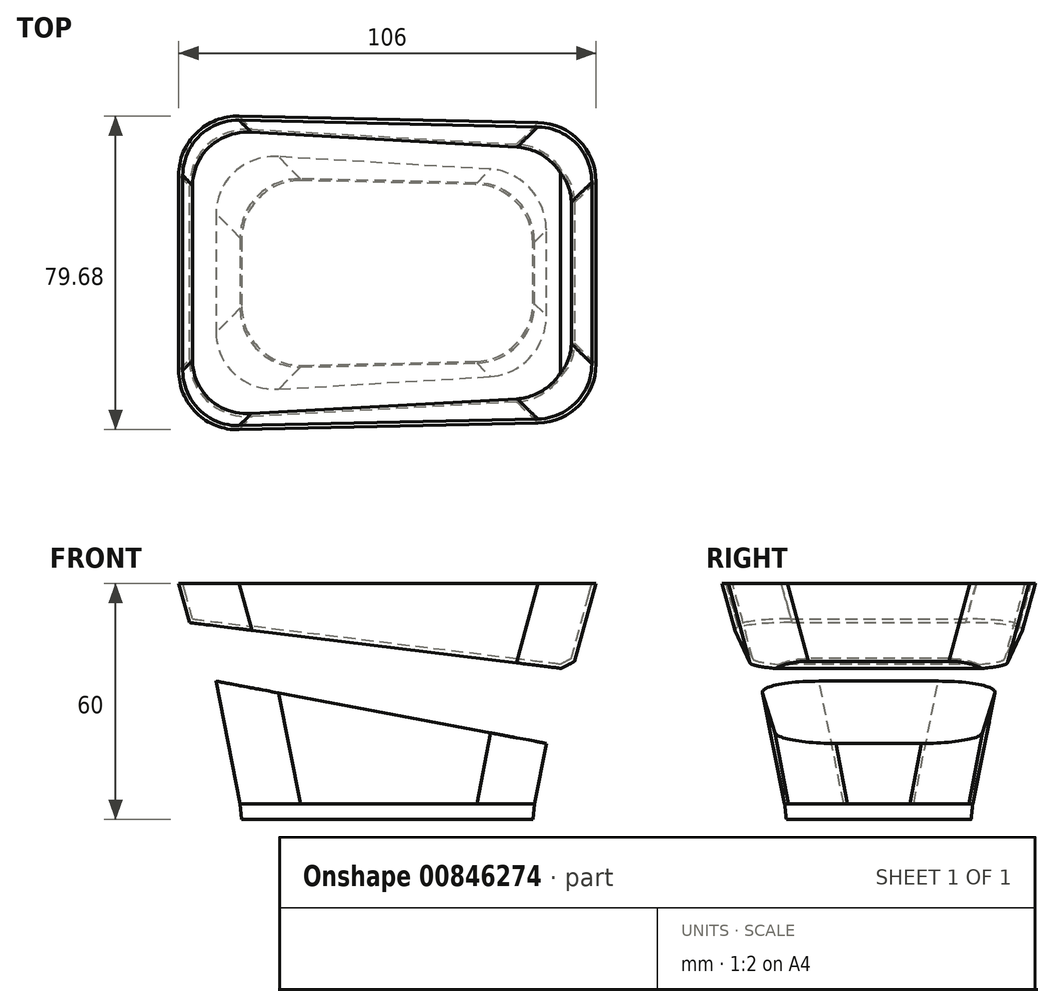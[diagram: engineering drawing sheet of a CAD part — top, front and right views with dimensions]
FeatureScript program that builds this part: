
annotation { "Feature Type Name" : "Feature", "Feature Type Description" : "" }
export const myFeature = defineFeature(function(context is Context, id is Id, definition is map)
    precondition{}
    {
        {
            var Q0;
            Q0=qCreatedBy(makeId("Top.planeOp"),FACE);
            var sketch = newSketch(context, id + "F0", { "sketchPlane" : qUnion([Q0])});
            skLineSegment(sketch, "E0", {"start": v(-45, 32) * mm, "end": v(-45, -32) * mm});
            skLineSegment(sketch, "E1", {"start": v(-45, -32) * mm, "end": v(45, -30) * mm});
            skLineSegment(sketch, "E2", {"start": v(45, -30) * mm, "end": v(45, 30) * mm});
            skLineSegment(sketch, "E3", {"start": v(45, 30) * mm, "end": v(-45, 32) * mm});
            skLineSegment(sketch, "E4.0", {"start": v(22.33, 22.5) * mm, "end": v(-21.67, 23.48) * mm});
            skLineSegment(sketch, "E4.1", {"start": v(37, -7.5) * mm, "end": v(37, 7.5) * mm});
            skLineSegment(sketch, "E4.2", {"start": v(-21.67, -23.48) * mm, "end": v(22.33, -22.5) * mm});
            skLineSegment(sketch, "E4.3", {"start": v(-37, 8.48) * mm, "end": v(-37, -8.48) * mm});
            skPoint(sketch, "E5.visualSharp", {"position": v(-37, 23.82) * mm});
            skArc(sketch, "E5.filletArc", {"start": v(-21.67, 23.48) * mm, "mid": v(-32.49, 19.2) * mm, "end": v(-37, 8.48) * mm});
            skPoint(sketch, "E6.visualSharp", {"position": v(-37, -23.82) * mm});
            skArc(sketch, "E6.filletArc", {"start": v(-37, -8.48) * mm, "mid": v(-32.49, -19.2) * mm, "end": v(-21.67, -23.48) * mm});
            skPoint(sketch, "E7.visualSharp", {"position": v(37, 22.18) * mm});
            skArc(sketch, "E7.filletArc", {"start": v(37, 7.5) * mm, "mid": v(32.72, 18) * mm, "end": v(22.33, 22.5) * mm});
            skPoint(sketch, "E8.visualSharp", {"position": v(37, -22.18) * mm});
            skArc(sketch, "E8.filletArc", {"start": v(22.33, -22.5) * mm, "mid": v(32.72, -18) * mm, "end": v(37, -7.5) * mm});
            skSolve(sketch);
        }
        {
            var Q0;
            Q0=qCreatedBy(makeId("Top.planeOp"),FACE);
            cPlane(context, id + "F1", {"entities" : qUnion([Q0]), "cplaneType" : CPlaneType.OFFSET, "offset" : 60 * mm, "width" : 150 * mm, "height" : 150 * mm});
        }
        {
            var Q0;
            Q0=qCreatedBy(id+"F1.planeOp",FACE);
            var sketch = newSketch(context, id + "F2", { "sketchPlane" : qUnion([Q0])});
            skLineSegment(sketch, "E9.1", {"start": v(38.33, 38.15) * mm, "end": v(-37.67, 39.84) * mm});
            skLineSegment(sketch, "E9.2", {"start": v(-53, 24.84) * mm, "end": v(-53, -24.84) * mm});
            skLineSegment(sketch, "E9.5", {"start": v(-37.67, -39.84) * mm, "end": v(38.33, -38.15) * mm});
            skLineSegment(sketch, "E9.7", {"start": v(53, -23.15) * mm, "end": v(53, 23.15) * mm});
            skPoint(sketch, "E10.visualSharp", {"position": v(-53, 40.18) * mm});
            skArc(sketch, "E10.filletArc", {"start": v(-37.67, 39.84) * mm, "mid": v(-48.49, 35.57) * mm, "end": v(-53, 24.84) * mm});
            skPoint(sketch, "E11.visualSharp", {"position": v(53, 37.82) * mm});
            skArc(sketch, "E11.filletArc", {"start": v(53, 23.15) * mm, "mid": v(48.72, 33.64) * mm, "end": v(38.33, 38.15) * mm});
            skPoint(sketch, "E12.visualSharp", {"position": v(53, -37.82) * mm});
            skArc(sketch, "E12.filletArc", {"start": v(38.33, -38.15) * mm, "mid": v(48.72, -33.64) * mm, "end": v(53, -23.15) * mm});
            skPoint(sketch, "E13.visualSharp", {"position": v(-53, -40.18) * mm});
            skArc(sketch, "E13.filletArc", {"start": v(-53, -24.84) * mm, "mid": v(-48.49, -35.57) * mm, "end": v(-37.67, -39.84) * mm});
            skSolve(sketch);
        }
        {
            var Q0;
            Q0=qCreatedBy(makeId("Front.planeOp"),FACE);
            var sketch = newSketch(context, id + "F3", { "sketchPlane" : qUnion([Q0])});
            skLineSegment(sketch, "E14", {"start": v(-37, 0) * mm, "end": v(-37.4, 4) * mm});
            skLineSegment(sketch, "E15", {"start": v(-37.4, 4) * mm, "end": v(-46.35, 49.51) * mm});
            skLineSegment(sketch, "E16", {"start": v(37, 0) * mm, "end": v(-37, 0) * mm});
            skLineSegment(sketch, "E17", {"start": v(-50.32, 50) * mm, "end": v(-53, 60) * mm});
            skLineSegment(sketch, "E18", {"start": v(-53, 60) * mm, "end": v(53, 60) * mm});
            skLineSegment(sketch, "E19", {"start": v(53, 60) * mm, "end": v(47.1, 38) * mm});
            skLineSegment(sketch, "E20", {"start": v(-50.32, 50) * mm, "end": v(47.1, 38) * mm});
            skLineSegment(sketch, "E21", {"start": v(37.4, 4) * mm, "end": v(37, 0) * mm});
            skLineSegment(sketch, "E22", {"start": v(44.16, 38.36) * mm, "end": v(37.4, 4) * mm});
            skLineSegment(sketch, "E23", {"start": v(-37.4, 4) * mm, "end": v(37.4, 4) * mm});
            skLineSegment(sketch, "E24", {"start": v(-50.32, 50) * mm, "end": v(-64.72, 39.12) * mm});
            skLineSegment(sketch, "E25", {"start": v(-64.72, 39.12) * mm, "end": v(67.69, 14.16) * mm});
            skLineSegment(sketch, "E26", {"start": v(67.69, 14.16) * mm, "end": v(47.1, 38) * mm});
            skLineSegment(sketch, "E27", {"start": v(44.16, 38.36) * mm, "end": v(47.7, 40.22) * mm});
            skSolve(sketch);
        }
        {
            var Q0;
            Q0=sQuery(id+"F3.wireOp",EDGE,"E23");
            var Q1;
            Q1=qCreatedBy(makeId("Top.planeOp"),FACE);
            cPlane(context, id + "F4", {"entities" : qUnion([Q0, Q1]), "cplaneType" : CPlaneType.LINE_ANGLE, "offset" : 25 * mm, "angle" : 0 * degree, "width" : 150 * mm, "height" : 150 * mm});
        }
        {
            var Q0;
            Q0=qCreatedBy(id+"F4.planeOp",FACE);
            var sketch = newSketch(context, id + "F5", { "sketchPlane" : qUnion([Q0])});
            skLineSegment(sketch, "E28.0", {"start": v(-37.4, -8.9) * mm, "end": v(-37.4, 8.9) * mm});
            skLineSegment(sketch, "E29.0", {"start": v(22.73, -22.9) * mm, "end": v(-22.07, -23.89) * mm});
            skLineSegment(sketch, "E30.0", {"start": v(37.4, 7.9) * mm, "end": v(37.4, -7.9) * mm});
            skLineSegment(sketch, "E31.0", {"start": v(-22.07, 23.89) * mm, "end": v(22.73, 22.9) * mm});
            skPoint(sketch, "E32.visualSharp", {"position": v(-37.4, -24.23) * mm});
            skArc(sketch, "E32.filletArc", {"start": v(-37.4, -8.9) * mm, "mid": v(-32.89, -19.62) * mm, "end": v(-22.07, -23.89) * mm});
            skPoint(sketch, "E33.visualSharp", {"position": v(37.4, -22.57) * mm});
            skArc(sketch, "E33.filletArc", {"start": v(22.73, -22.9) * mm, "mid": v(33.12, -18.38) * mm, "end": v(37.4, -7.9) * mm});
            skPoint(sketch, "E34.visualSharp", {"position": v(37.4, 22.57) * mm});
            skArc(sketch, "E34.filletArc", {"start": v(37.4, 7.9) * mm, "mid": v(33.12, 18.38) * mm, "end": v(22.73, 22.9) * mm});
            skPoint(sketch, "E35.visualSharp", {"position": v(-37.4, 24.23) * mm});
            skArc(sketch, "E35.filletArc", {"start": v(-22.07, 23.89) * mm, "mid": v(-32.89, 19.62) * mm, "end": v(-37.4, 8.9) * mm});
            skSolve(sketch);
        }
        {
            var Q0;
            Q0=makeQuery(id+"F0.imprint","IMPRINT",FACE,{"disambiguationData":[TD([[makeQuery(id+"F0.imprint","IMPRINT",EDGE,{"derivedFrom":sQuery(id+"F0.wireOp",EDGE,"E4.0")}),1.0]])]});
            var Q1;
            Q1=makeQuery(id+"F5.imprint","IMPRINT",FACE,{"disambiguationData":[TD([[makeQuery(id+"F5.imprint","IMPRINT",EDGE,{"derivedFrom":sQuery(id+"F5.wireOp",EDGE,"E28.0")}),-1.0]])]});
            loft(context, id + "F6", {"sheetProfilesArray" : [{ "sheetProfileEntities" : qUnion([Q0]) }, { "sheetProfileEntities" : qUnion([Q1]) }]});
        }
        {
            var Q0;
            Q0=sQuery(id+"F3.wireOp",VERTEX,"E15.end");
            var Q1;
            Q1=qCreatedBy(makeId("Top.planeOp"),FACE);
            cPlane(context, id + "F7", {"entities" : qUnion([Q0, Q1]), "cplaneType" : CPlaneType.PLANE_POINT, "offset" : 25 * mm, "width" : 150 * mm, "height" : 150 * mm});
        }
        {
            var Q0;
            Q0=qCreatedBy(id+"F7.planeOp",FACE);
            var sketch = newSketch(context, id + "F8", { "sketchPlane" : qUnion([Q0])});
            skLineSegment(sketch, "E36.0", {"start": v(-46.32, 18.01) * mm, "end": v(-46.32, -18.01) * mm});
            skLineSegment(sketch, "E37.0", {"start": v(31.65, 31.62) * mm, "end": v(-30.99, 33) * mm});
            skLineSegment(sketch, "E38.0", {"start": v(46.32, -16.62) * mm, "end": v(46.32, 16.62) * mm});
            skLineSegment(sketch, "E39.0", {"start": v(-30.99, -33) * mm, "end": v(31.65, -31.62) * mm});
            skPoint(sketch, "E40.visualSharp", {"position": v(46.32, 31.3) * mm});
            skArc(sketch, "E40.filletArc", {"start": v(46.32, 16.62) * mm, "mid": v(42.04, 27.1) * mm, "end": v(31.65, 31.62) * mm});
            skPoint(sketch, "E41.visualSharp", {"position": v(46.32, -31.3) * mm});
            skArc(sketch, "E41.filletArc", {"start": v(31.65, -31.62) * mm, "mid": v(42.04, -27.1) * mm, "end": v(46.32, -16.62) * mm});
            skPoint(sketch, "E42.visualSharp", {"position": v(-46.32, -33.35) * mm});
            skArc(sketch, "E42.filletArc", {"start": v(-46.32, -18.01) * mm, "mid": v(-41.8, -28.74) * mm, "end": v(-30.99, -33) * mm});
            skPoint(sketch, "E43.visualSharp", {"position": v(-46.32, 33.35) * mm});
            skArc(sketch, "E43.filletArc", {"start": v(-30.99, 33) * mm, "mid": v(-41.8, 28.74) * mm, "end": v(-46.32, 18.01) * mm});
            skSolve(sketch);
        }
        {
            var Q1;
            Q1=makeQuery(id+"F6.opLoft","CAP_FACE",FACE,{"disambiguationData":[OSD([makeQuery(id+"F5.imprint","IMPRINT",FACE,{"disambiguationData":[TD([[makeQuery(id+"F5.imprint","IMPRINT",EDGE,{"derivedFrom":sQuery(id+"F5.wireOp",EDGE,"E28.0")}),-1.0]])]})])],"isStart":true});
            var Q2;
            Q2=makeQuery(id+"F8.imprint","IMPRINT",FACE,{"disambiguationData":[TD([[makeQuery(id+"F8.imprint","IMPRINT",EDGE,{"derivedFrom":sQuery(id+"F8.wireOp",EDGE,"E36.0")}),1.0]])]});
            loft(context, id + "F9", {"operationType" : NewBodyOperationType.ADD, "sheetProfilesArray" : [{ "sheetProfileEntities" : qUnion([Q1]) }, { "sheetProfileEntities" : qUnion([Q2]) }]});
        }
        {
            var Q0;
            {var subQ2=sQuery(id+"F3.wireOp",EDGE,"E17");Q0=makeQuery(id+"F3.imprint","IMPRINT",FACE,{"disambiguationData":[TD([[makeQuery(id+"F3.imprint","IMPRINT",EDGE,{"derivedFrom":subQ2}),-1.0]])]});}
            extrude(context, id + "F10", {"entities" : qUnion([Q0]), "operationType" : NewBodyOperationType.REMOVE, "endBound" : BoundingType.SYMMETRIC, "depth" : 80 * mm, "offsetDistance" : 25 * mm});
        }
        {
            var Q0;
            Q0=qCreatedBy(makeId("Top.planeOp"),FACE);
            var Q1;
            Q1=sQuery(id+"F3.wireOp",VERTEX,"E20.end");
            cPlane(context, id + "F11", {"entities" : qUnion([Q0, Q1]), "cplaneType" : CPlaneType.PLANE_POINT, "offset" : 25 * mm, "width" : 150 * mm, "height" : 150 * mm});
        }
        {
            var Q0;
            Q0=qCreatedBy(id+"F11.planeOp",FACE);
            var sketch = newSketch(context, id + "F12", { "sketchPlane" : qUnion([Q0])});
            skLineSegment(sketch, "E44.0", {"start": v(47, -17.28) * mm, "end": v(47, 17.28) * mm});
            skLineSegment(sketch, "E45.0", {"start": v(-46.99, 18.7) * mm, "end": v(-46.99, -18.7) * mm});
            skLineSegment(sketch, "E46.0", {"start": v(-31.66, -33.7) * mm, "end": v(32.33, -32.27) * mm});
            skLineSegment(sketch, "E47.0", {"start": v(32.33, 32.27) * mm, "end": v(-31.66, 33.7) * mm});
            skPoint(sketch, "E48.visualSharp", {"position": v(-46.99, 34.03) * mm});
            skArc(sketch, "E48.filletArc", {"start": v(-31.66, 33.7) * mm, "mid": v(-42.48, 29.42) * mm, "end": v(-46.99, 18.7) * mm});
            skPoint(sketch, "E49.visualSharp", {"position": v(47, 31.95) * mm});
            skArc(sketch, "E49.filletArc", {"start": v(47, 17.28) * mm, "mid": v(42.72, 27.76) * mm, "end": v(32.33, 32.27) * mm});
            skPoint(sketch, "E50.visualSharp", {"position": v(47, -31.95) * mm});
            skArc(sketch, "E50.filletArc", {"start": v(32.33, -32.27) * mm, "mid": v(42.72, -27.76) * mm, "end": v(47, -17.28) * mm});
            skPoint(sketch, "E51.visualSharp", {"position": v(-47, -34.03) * mm});
            skArc(sketch, "E51.filletArc", {"start": v(-46.99, -18.7) * mm, "mid": v(-42.48, -29.42) * mm, "end": v(-31.66, -33.7) * mm});
            skSolve(sketch);
        }
        {
            var Q1;
            Q1=makeQuery(id+"F2.imprint","IMPRINT",FACE,{"disambiguationData":[TD([[makeQuery(id+"F2.imprint","IMPRINT",EDGE,{"derivedFrom":sQuery(id+"F2.wireOp",EDGE,"E9.1")}),1.0]])]});
            var Q2;
            Q2=makeQuery(id+"F12.imprint","IMPRINT",FACE,{"disambiguationData":[TD([[makeQuery(id+"F12.imprint","IMPRINT",EDGE,{"derivedFrom":sQuery(id+"F12.wireOp",EDGE,"E44.0")}),1.0]])]});
            loft(context, id + "F13", {"sheetProfilesArray" : [{ "sheetProfileEntities" : qUnion([Q1]) }, { "sheetProfileEntities" : qUnion([Q2]) }]});
        }
        {
            var Q0;
            {var subQ0=sQuery(id+"F3.wireOp",EDGE,"E26");Q0=makeQuery(id+"F3.imprint","IMPRINT",FACE,{"disambiguationData":[TD([[makeQuery(id+"F3.imprint","IMPRINT",EDGE,{"derivedFrom":subQ0}),1.0]])]});}
            var Q1;
            {var subQ0=sQuery(id+"F3.wireOp",EDGE,"E20");var subQ1=sQuery(id+"F3.wireOp",EDGE,"E15");var subQ2=makeQuery(id+"F3.imprint","INTERSECT",VERTEX,{"derivedFrom":[subQ1,subQ0]});Q1=makeQuery(id+"F3.imprint","IMPRINT",FACE,{"disambiguationData":[TD([[makeQuery(id+"F3.imprint","IMPRINT",EDGE,{"disambiguationData":[TD([[subQ2,1.0]])],"derivedFrom":subQ1}),-1.0]])]});}
            var Q2;
            {var subQ5=sQuery(id+"F3.wireOp",EDGE,"E24");Q2=makeQuery(id+"F3.imprint","IMPRINT",FACE,{"disambiguationData":[TD([[makeQuery(id+"F3.imprint","IMPRINT",EDGE,{"derivedFrom":subQ5}),1.0]])]});}
            var Q3;
            {var subQ3=sQuery(id+"F3.wireOp",EDGE,"E27");Q3=makeQuery(id+"F3.imprint","IMPRINT",FACE,{"disambiguationData":[TD([[makeQuery(id+"F3.imprint","IMPRINT",EDGE,{"derivedFrom":subQ3}),-1.0]])]});}
            extrude(context, id + "F14", {"entities" : qUnion([Q0, Q1, Q2, Q3]), "operationType" : NewBodyOperationType.REMOVE, "endBound" : BoundingType.SYMMETRIC, "oppositeDirection" : true, "depth" : 80 * mm, "offsetDistance" : 25 * mm});
        }
        {
            var Q0;
            Q0=makeQuery(id+"F13.opLoft","CAP_FACE",FACE,{"disambiguationData":[OSD([makeQuery(id+"F2.imprint","IMPRINT",FACE,{"disambiguationData":[TD([[makeQuery(id+"F2.imprint","IMPRINT",EDGE,{"derivedFrom":sQuery(id+"F2.wireOp",EDGE,"E9.1")}),1.0]])]})])],"isStart":true});
            shell(context, id + "F15", {"entities" : qUnion([Q0]), "thickness" : 1 * mm});
        }
    });
